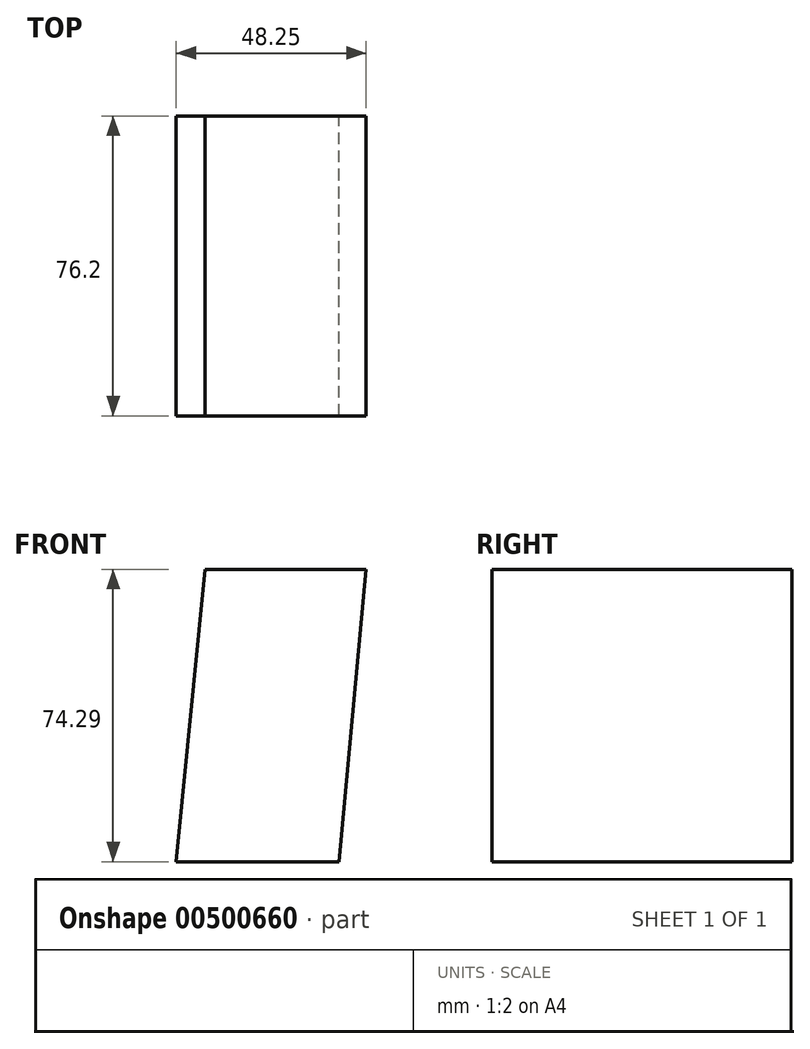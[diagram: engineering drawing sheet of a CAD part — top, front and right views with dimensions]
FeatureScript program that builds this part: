
annotation { "Feature Type Name" : "Feature", "Feature Type Description" : "" }
export const myFeature = defineFeature(function(context is Context, id is Id, definition is map)
    precondition{}
    {
        {
            var Q0;
            Q0=qCreatedBy(makeId("Front.planeOp"),FACE);
            var sketch = newSketch(context, id + "F0", { "sketchPlane" : qUnion([Q0])});
            skLineSegment(sketch, "E0.bottom", {"start": v(-17.53, 65.27) * mm, "end": v(23.37, 65.27) * mm});
            skLineSegment(sketch, "E0.top", {"start": v(-24.88, -9.02) * mm, "end": v(16.42, -9.02) * mm});
            skLineSegment(sketch, "E1", {"start": v(-24.88, -9.02) * mm, "end": v(-17.53, 65.27) * mm});
            skLineSegment(sketch, "E2", {"start": v(23.37, 65.27) * mm, "end": v(16.42, -9.02) * mm});
            skLineSegment(sketch, "E3", {"start": v(-17.53, 65.27) * mm, "end": v(-17.53, -9.02) * mm});
            skLineSegment(sketch, "E4", {"start": v(16.42, -9.02) * mm, "end": v(16.42, 65.27) * mm});
            skSolve(sketch);
        }
        {
            var Q0;
            {var subQ0=sQuery(id+"F0.wireOp",EDGE,"E3");Q0=makeQuery(id+"F0.imprint","IMPRINT",FACE,{"disambiguationData":[TD([[makeQuery(id+"F0.imprint","IMPRINT",EDGE,{"derivedFrom":subQ0}),1.0]])]});}
            var Q1;
            {var subQ0=sQuery(id+"F0.wireOp",EDGE,"E2");Q1=makeQuery(id+"F0.imprint","IMPRINT",FACE,{"disambiguationData":[TD([[makeQuery(id+"F0.imprint","IMPRINT",EDGE,{"derivedFrom":subQ0}),-1.0]])]});}
            var Q2;
            {var subQ0=sQuery(id+"F0.wireOp",EDGE,"E1");Q2=makeQuery(id+"F0.imprint","IMPRINT",FACE,{"disambiguationData":[TD([[makeQuery(id+"F0.imprint","IMPRINT",EDGE,{"derivedFrom":subQ0}),-1.0]])]});}
            extrude(context, id + "F1", {"entities" : qUnion([Q0, Q1, Q2]), "depth" : 76.2 * mm});
        }
    });
